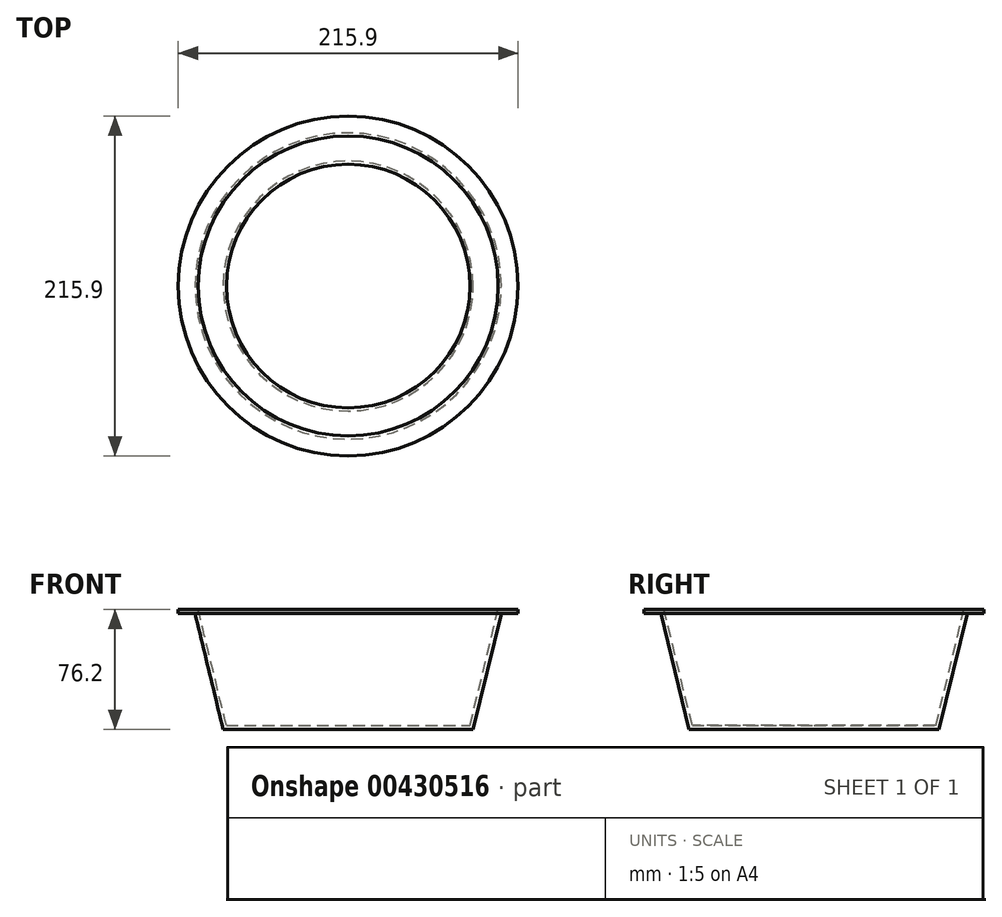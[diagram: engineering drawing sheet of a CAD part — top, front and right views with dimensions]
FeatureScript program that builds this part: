
annotation { "Feature Type Name" : "Feature", "Feature Type Description" : "" }
export const myFeature = defineFeature(function(context is Context, id is Id, definition is map)
    precondition{}
    {
        {
            var Q0;
            Q0=qCreatedBy(makeId("Front.planeOp"),FACE);
            var sketch = newSketch(context, id + "F0", { "sketchPlane" : qUnion([Q0])});
            skLineSegment(sketch, "E0.0", {"start": v(-79.38, -76.2) * mm, "end": v(0, -76.2) * mm});
            skLineSegment(sketch, "E0.1", {"start": v(-97.25, -2.54) * mm, "end": v(-79.38, -76.2) * mm});
            skLineSegment(sketch, "E0.2", {"start": v(-97.25, -2.54) * mm, "end": v(-107.95, -2.54) * mm});
            skLineSegment(sketch, "E1.1", {"start": v(-77.38, -73.66) * mm, "end": v(0, -73.66) * mm});
            skLineSegment(sketch, "E1.2", {"start": v(-95.25, 0) * mm, "end": v(-77.38, -73.66) * mm});
            skLineSegment(sketch, "E1.3", {"start": v(-95.25, 0) * mm, "end": v(-107.95, 0) * mm});
            skLineSegment(sketch, "E2", {"start": v(0, -76.2) * mm, "end": v(0, -73.66) * mm});
            skLineSegment(sketch, "E3", {"start": v(-107.95, 0) * mm, "end": v(-107.95, -2.54) * mm});
            skSolve(sketch);
        }
        {
            var Q0;
            Q0=makeQuery(id+"F0.imprint","IMPRINT",FACE,{"disambiguationData":[TD([[makeQuery(id+"F0.imprint","IMPRINT",EDGE,{"derivedFrom":sQuery(id+"F0.wireOp",EDGE,"E0.0")}),1.0]])]});
            var Q1;
            Q1=sQuery(id+"F0.wireOp",EDGE,"E2");
            revolve(context, id + "F1", {"entities" : qUnion([Q0]), "axis" : qUnion([Q1]), "revolveType" : RevolveType.FULL});
        }
    });
